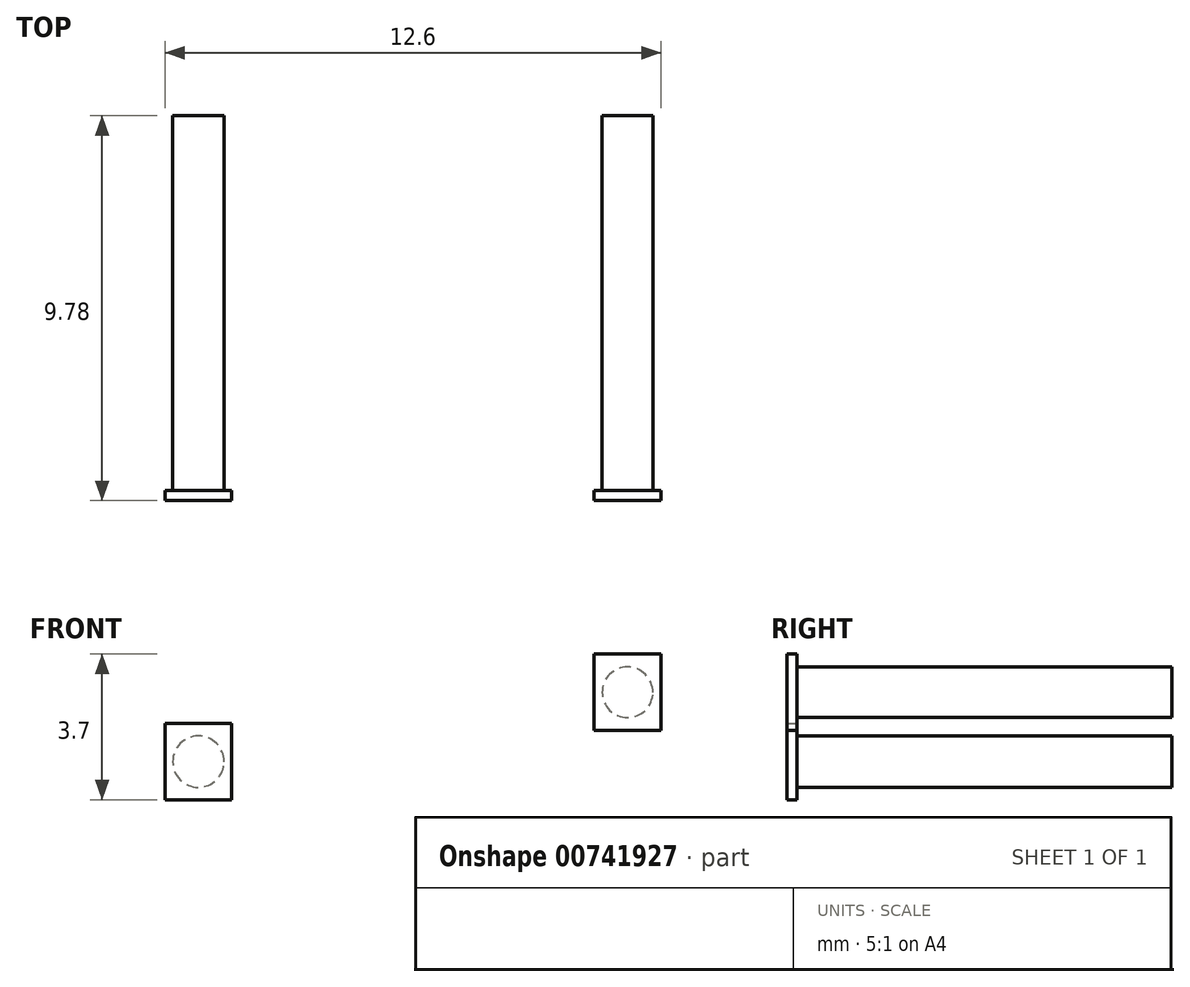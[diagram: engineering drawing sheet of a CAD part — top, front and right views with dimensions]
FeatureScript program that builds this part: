
annotation { "Feature Type Name" : "Feature", "Feature Type Description" : "" }
export const myFeature = defineFeature(function(context is Context, id is Id, definition is map)
    precondition{}
    {
        {
            var Q0;
            Q0=qCreatedBy(makeId("Front.planeOp"),FACE);
            var sketch = newSketch(context, id + "F0", { "sketchPlane" : qUnion([Q0])});
            skCircle(sketch, "E0", {"center": v(-25.97, 39.42) * mm, "radius": 0.65 * mm});
            skCircle(sketch, "E1", {"center": v(-21.57, 39.66) * mm, "radius": 0.64 * mm});
            skCircle(sketch, "E2", {"center": v(-32.47, 37.9) * mm, "radius": 0.65 * mm});
            skSolve(sketch);
        }
        {
            var Q0;
            Q0=makeQuery(id+"F0.imprint","IMPRINT",FACE,{"disambiguationData":[TD([[makeQuery(id+"F0.imprint","IMPRINT",EDGE,{"derivedFrom":sQuery(id+"F0.wireOp",EDGE,"E1")}),1.0]])]});
            var Q1;
            Q1=makeQuery(id+"F0.imprint","IMPRINT",FACE,{"disambiguationData":[TD([[makeQuery(id+"F0.imprint","IMPRINT",EDGE,{"derivedFrom":sQuery(id+"F0.wireOp",EDGE,"E2")}),1.0]])]});
            extrude(context, id + "F1", {"entities" : qUnion([Q0, Q1]), "depth" : 9.52 * mm});
        }
        {
            var Q0;
            Q0=makeQuery(id+"F1.opExtrude","CAP_FACE",FACE,{"disambiguationData":[OSD([sQuery(id+"F0.wireOp",EDGE,"E2")])],"isStart":false});
            var sketch = newSketch(context, id + "F2", { "sketchPlane" : qUnion([Q0])});
            skCircle(sketch, "E3.0", {"center": v(-32.47, 37.9) * mm, "radius": 0.65 * mm});
            skCircle(sketch, "E4.0", {"center": v(-21.57, 39.66) * mm, "radius": 0.64 * mm});
            skLineSegment(sketch, "E5.bottom", {"start": v(-31.63, 38.87) * mm, "end": v(-33.32, 38.87) * mm});
            skLineSegment(sketch, "E5.top", {"start": v(-31.63, 36.93) * mm, "end": v(-33.32, 36.93) * mm});
            skLineSegment(sketch, "E5.left", {"start": v(-31.63, 38.87) * mm, "end": v(-31.63, 36.93) * mm});
            skLineSegment(sketch, "E5.right", {"start": v(-33.32, 38.87) * mm, "end": v(-33.32, 36.93) * mm});
            skLineSegment(sketch, "E6.bottom", {"start": v(-20.72, 40.63) * mm, "end": v(-22.42, 40.63) * mm});
            skLineSegment(sketch, "E6.top", {"start": v(-20.72, 38.7) * mm, "end": v(-22.42, 38.7) * mm});
            skLineSegment(sketch, "E6.left", {"start": v(-20.72, 40.63) * mm, "end": v(-20.72, 38.7) * mm});
            skLineSegment(sketch, "E6.right", {"start": v(-22.42, 40.63) * mm, "end": v(-22.42, 38.7) * mm});
            skSolve(sketch);
        }
        {
            var Q0;
            Q0 = qSketchRegion(id + "F2", true);
            var Q1;
            Q1=makeQuery(id+"F2.imprint","IMPRINT",FACE,{"disambiguationData":[TD([[makeQuery(id+"F2.imprint","IMPRINT",EDGE,{"derivedFrom":sQuery(id+"F2.wireOp",EDGE,"E4.0")}),1.0]])]});
            var Q2;
            Q2=makeQuery(id+"F2.imprint","IMPRINT",FACE,{"disambiguationData":[TD([[makeQuery(id+"F2.imprint","IMPRINT",EDGE,{"derivedFrom":sQuery(id+"F2.wireOp",EDGE,"E3.0")}),1.0]])]});
            extrude(context, id + "F3", {"entities" : qUnion([Q0, Q1, Q2]), "operationType" : NewBodyOperationType.ADD, "depth" : 0.25 * mm, "offsetDistance" : 25.4 * mm});
        }
    });
